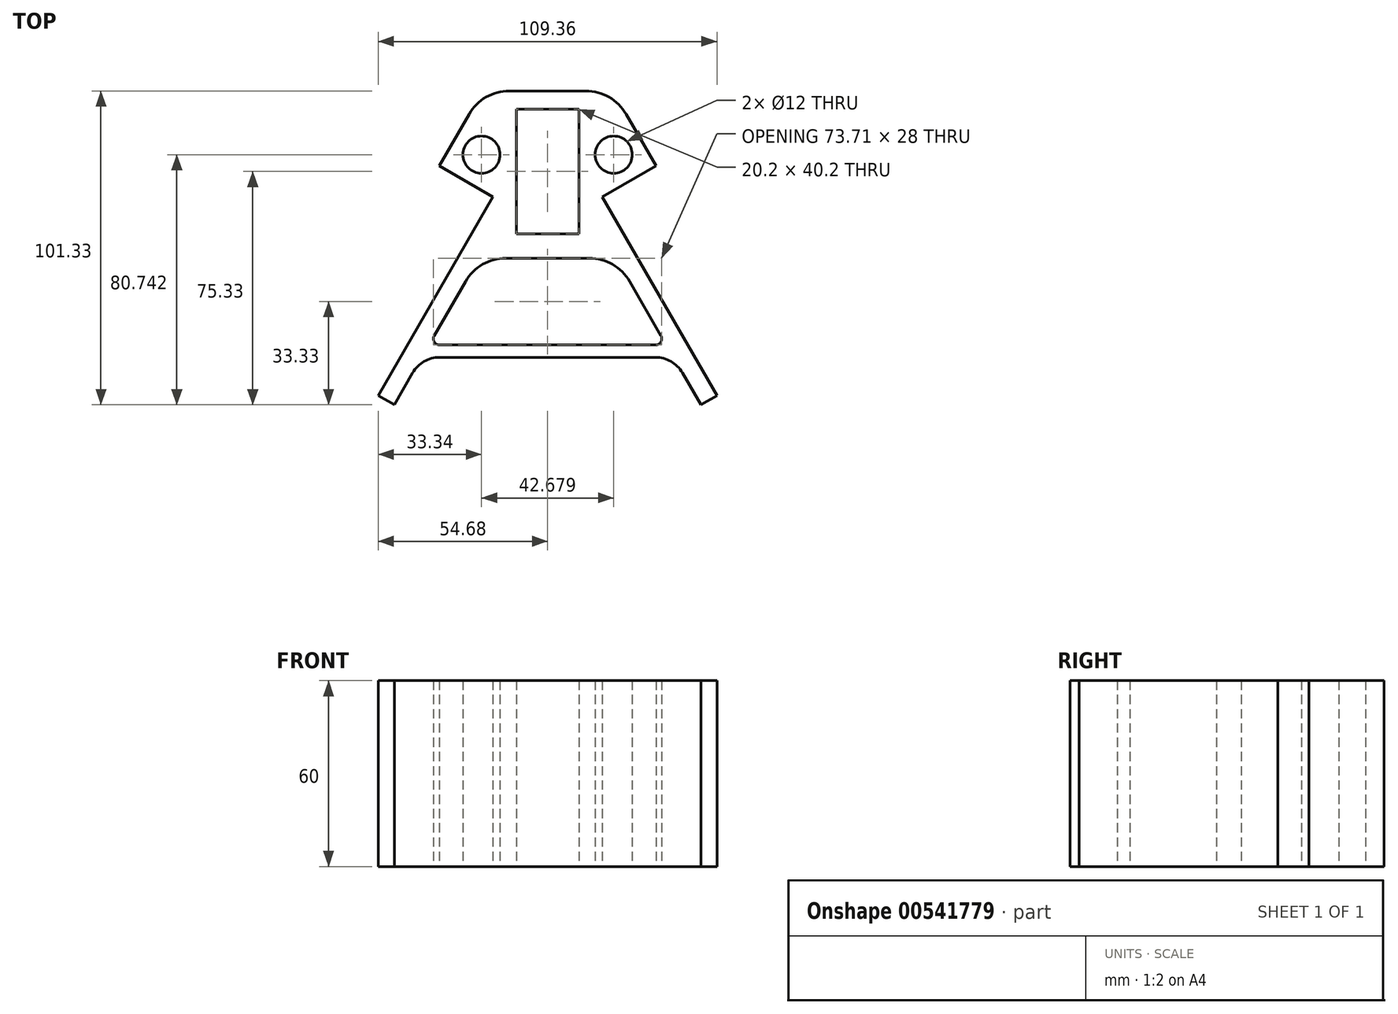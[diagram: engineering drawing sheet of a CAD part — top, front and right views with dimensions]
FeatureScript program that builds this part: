
annotation { "Feature Type Name" : "Feature", "Feature Type Description" : "" }
export const myFeature = defineFeature(function(context is Context, id is Id, definition is map)
    precondition{}
    {
        {
            var Q0;
            Q0=qCreatedBy(makeId("Top.planeOp"),FACE);
            var sketch = newSketch(context, id + "F0", { "sketchPlane" : qUnion([Q0])});
            skLineSegment(sketch, "E0", {"start": v(-35, 1.75) * mm, "end": v(-25.33, 18.5) * mm});
            skLineSegment(sketch, "E1", {"start": v(-12.34, 26) * mm, "end": v(12.34, 26) * mm});
            skLineSegment(sketch, "E2", {"start": v(25.33, 18.5) * mm, "end": v(35, 1.75) * mm});
            skLineSegment(sketch, "E3", {"start": v(35, 1.75) * mm, "end": v(17.68, -8.25) * mm});
            skLineSegment(sketch, "E4", {"start": v(17.68, -8.25) * mm, "end": v(54.68, -72.33) * mm});
            skLineSegment(sketch, "E5", {"start": v(54.68, -72.33) * mm, "end": v(49.48, -75.33) * mm});
            skLineSegment(sketch, "E6", {"start": v(49.48, -75.33) * mm, "end": v(43.52, -65) * mm});
            skLineSegment(sketch, "E7", {"start": v(34.86, -60) * mm, "end": v(-34.86, -60) * mm});
            skLineSegment(sketch, "E8", {"start": v(-43.52, -65) * mm, "end": v(-49.48, -75.33) * mm});
            skLineSegment(sketch, "E9", {"start": v(-49.48, -75.33) * mm, "end": v(-54.68, -72.33) * mm});
            skLineSegment(sketch, "E10", {"start": v(-54.68, -72.33) * mm, "end": v(-17.68, -8.25) * mm});
            skLineSegment(sketch, "E11", {"start": v(-17.68, -8.25) * mm, "end": v(-35, 1.75) * mm});
            skLineSegment(sketch, "E12.bottom", {"start": v(10.1, 20.1) * mm, "end": v(-10.1, 20.1) * mm});
            skLineSegment(sketch, "E12.top", {"start": v(10.1, -20.1) * mm, "end": v(-10.1, -20.1) * mm});
            skLineSegment(sketch, "E12.left", {"start": v(10.1, 20.1) * mm, "end": v(10.1, -20.1) * mm});
            skLineSegment(sketch, "E12.right", {"start": v(-10.1, 20.1) * mm, "end": v(-10.1, -20.1) * mm});
            skPoint(sketch, "E12.middle", {"position": v(0, 0) * mm});
            skLineSegment(sketch, "E13", {"start": v(-13.5, -28) * mm, "end": v(13.5, -28) * mm});
            skLineSegment(sketch, "E14", {"start": v(26.48, -35.5) * mm, "end": v(36.59, -53) * mm});
            skLineSegment(sketch, "E15", {"start": v(34.86, -56) * mm, "end": v(-34.86, -56) * mm});
            skLineSegment(sketch, "E16", {"start": v(-36.59, -53) * mm, "end": v(-26.48, -35.5) * mm});
            skPoint(sketch, "E17.visualSharp", {"position": v(-21, 26) * mm});
            skArc(sketch, "E17.filletArc", {"start": v(-12.34, 26) * mm, "mid": v(-19.84, 24) * mm, "end": v(-25.33, 18.5) * mm});
            skPoint(sketch, "E18.visualSharp", {"position": v(21, 26) * mm});
            skArc(sketch, "E18.filletArc", {"start": v(25.33, 18.5) * mm, "mid": v(19.84, 24) * mm, "end": v(12.34, 26) * mm});
            skPoint(sketch, "E19.visualSharp", {"position": v(-22.15, -28) * mm});
            skArc(sketch, "E19.filletArc", {"start": v(-13.5, -28) * mm, "mid": v(-21, -30) * mm, "end": v(-26.48, -35.5) * mm});
            skPoint(sketch, "E20.visualSharp", {"position": v(22.15, -28) * mm});
            skArc(sketch, "E20.filletArc", {"start": v(26.48, -35.5) * mm, "mid": v(21, -30) * mm, "end": v(13.5, -28) * mm});
            skPoint(sketch, "E21.visualSharp", {"position": v(38.32, -56) * mm});
            skArc(sketch, "E21.filletArc", {"start": v(34.86, -56) * mm, "mid": v(36.59, -55) * mm, "end": v(36.59, -53) * mm});
            skPoint(sketch, "E22.visualSharp", {"position": v(-38.32, -56) * mm});
            skArc(sketch, "E22.filletArc", {"start": v(-36.59, -53) * mm, "mid": v(-36.59, -55) * mm, "end": v(-34.86, -56) * mm});
            skPoint(sketch, "E23.visualSharp", {"position": v(-40.63, -60) * mm});
            skArc(sketch, "E23.filletArc", {"start": v(-34.86, -60) * mm, "mid": v(-39.86, -61.34) * mm, "end": v(-43.52, -65) * mm});
            skPoint(sketch, "E24.visualSharp", {"position": v(40.63, -60) * mm});
            skArc(sketch, "E24.filletArc", {"start": v(43.52, -65) * mm, "mid": v(39.86, -61.34) * mm, "end": v(34.86, -60) * mm});
            skCircle(sketch, "E25", {"center": v(-21.34, 5.41) * mm, "radius": 6 * mm});
            skLineSegment(sketch, "E26", {"start": v(-21.34, 5.41) * mm, "end": v(-26.34, -3.25) * mm, "construction": true});
            skPoint(sketch, "E26.endSnap0", {"position": v(-26.34, -3.25) * mm});
            skCircle(sketch, "E27.MirrorC", {"center": v(21.34, 5.41) * mm, "radius": 6 * mm});
            skPoint(sketch, "E28", {"position": v(0, 10) * mm});
            skPoint(sketch, "E29", {"position": v(0, -10) * mm});
            skLineSegment(sketch, "E30", {"start": v(-21, 26) * mm, "end": v(34.64, 58.13) * mm, "construction": true});
            skLineSegment(sketch, "E31", {"start": v(-19.84, 24) * mm, "end": v(23.35, 48.92) * mm, "construction": true});
            skSolve(sketch);
        }
        {
            var Q0;
            Q0=makeQuery(id+"F0.imprint","IMPRINT",FACE,{"disambiguationData":[TD([[makeQuery(id+"F0.imprint","IMPRINT",EDGE,{"derivedFrom":sQuery(id+"F0.wireOp",EDGE,"E0")}),-1.0]])]});
            extrude(context, id + "F1", {"entities" : qUnion([Q0]), "depth" : 60 * mm, "offsetDistance" : 25 * mm});
        }
        {
            var Q0;
            Q0=makeQuery(id+"F1.opExtrude","SWEPT_FACE",FACE,{"disambiguationData":[OSD([sQuery(id+"F0.wireOp",EDGE,"E3")])]});
            var sketch = newSketch(context, id + "F2", { "sketchPlane" : qUnion([Q0])});
            skLineSegment(sketch, "E32", {"start": v(21.19, 60) * mm, "end": v(21.19, 0) * mm, "construction": true});
            skPoint(sketch, "E33", {"position": v(21.19, 50) * mm});
            skPoint(sketch, "E34", {"position": v(21.19, 10) * mm});
            skSolve(sketch);
        }
        {
            var Q0;
            Q0=makeQuery(id+"F1.opExtrude","SWEPT_FACE",FACE,{"disambiguationData":[OSD([sQuery(id+"F0.wireOp",EDGE,"E11")])]});
            var sketch = newSketch(context, id + "F3", { "sketchPlane" : qUnion([Q0])});
            skLineSegment(sketch, "E35", {"start": v(-21.19, 0) * mm, "end": v(-21.19, 60) * mm, "construction": true});
            skPoint(sketch, "E36", {"position": v(-21.19, 10) * mm});
            skPoint(sketch, "E37", {"position": v(-21.19, 50) * mm});
            skSolve(sketch);
        }
    });
